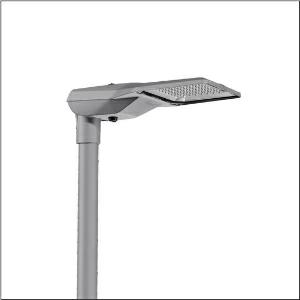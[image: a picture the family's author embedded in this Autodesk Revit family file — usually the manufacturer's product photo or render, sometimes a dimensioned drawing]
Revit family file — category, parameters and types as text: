
# Revit family: streetlight_sl_21_iq_midi___stw1_0a_5xe3e31y08mb_1dd4
name_source: partatom
category: Lighting Fixtures
units: mm (PartAtom-declared; Revit-internal decimal feet)

## family parameters
Cut with Voids When Loaded = No
Host = Face
Light Source = No
Part Type = Normal
Room Calculation Point = No
Round Connector Dimension = Use Diameter
Shared = No

## types (1)
- --- (1 x LED, 18340 lm, 129.3 W, 3000K)
    Apparent Load = 129 VA
    CIE Flux Codes = 38 75 98 100 100
    Color Rendering = 70
    Color Temperature = 3000K
    Default Elevation = 1800 mm
    Description = Streetlight SL 21 iQ midi, mast luminaire, primary light control with lens, of PMMA, primary optical cover: cover, of toughened safety glass, transparent, light distribution: STW1.0a, light emission: direct distribution, primary light characteristic: asymmetric, installation type: post-top, side-entry, LED, High Power LED, rated luminous flux: 18.340lm, luminous efficacy: 142lm/W, light colour: 730, colour temperature: 3000K, control: presetting dimming logarithmic, Street-Remote, Auto-Match, Temp-Guard, Lumen-Switch, Night-Set, Smart-Wire, Light-Fading, Desk-Remote (wireless, voltage-free reading and setting of iQ features in the workshop via application-optimized NFC function/RFID function), optimised constant luminous flux control (CLO 2.0), mains connection: 230..240V, AC, 50/60Hz, start of lifetime: 129W, end of service life: 142W, reduction: 56W, luminaire housing, of diecast aluminium, powder-coated, Siteco® metallic grey (DB 702S), corrosivity category C5 mid according to DIN EN ISO 12944, please order mast flange separately, inclination adjustable: 0°, 5°, 10°, 15°, sealing non-destructively replaceable, multi-level sealing system, length: 644mm, width: 335mm, height: 110mm, mast flange for spigot size: 42mm (side-entry): 5XC10008XM4, 60/48mm (side-entry/post-top): 5XC10108XM2, 76/60mm (side-entry/post-top): 5XC10108XM1, Smart Interface below and above, protection rating (complete): IP66, insulation class (complete): insulation class II (safety insulation), certification: CE, ENEC, ENEC+, VDE, impact resistance: IK09, permissible operating ambient temperature for outdoor applications: -40..+50°C, standard-compliant lighting for roads and squares, packaging unit: 1 piece

Light Distribution: STW1.0a
    Height = 111 mm
    Lamp = 1 x LED
    Lamp Light Flux = 18340 lm
    Lamp Power = 129.3 W
    Lamp count = 1
    Length = 644 mm
    Luminous efficacy = 142 lm/W
    Manufacturer = Siteco
    ModVariant = No
    Model = 5XE3E31Y08MB
    Number of Poles = 1
    OnlyDefault = Yes
    Power Factor = 1
    Product Name = Streetlight SL 21 iQ midi | STW1.0a
    Product group = mast luminaire | pylon top
    ProductGroupID = 6100
    Protection Class = Protection class II
    Protection Degree = IP 66
    RLX_Detail_Level = 1
    RLX_Emergency_Light_Flux = 0 lm
    RLX_Emergency_Type = 0
    RLX_Emergency_Type_DB = No
    RlxData = <blob elided: 91025 chars, md5=10f3e0e9>
    Socket = socket
    Standby Power = 0 W
    System Light Flux = 18340 lm
    System Power = 129 W
    Type Comments = factory setting: luminous flux: 100 % | dim-lin: 254 | 672 mA
    Type Image = l_1004304.jpg
    URL = http://relux.com
    VarID = @adj_044301
    Voltage = 0 V
    Weight = 0.00 kg
    Width = 336 mm

## geometry (parser evidence)
native form markers: Blend x4, Sweep x11
no freeform markers — native parametric forms only
